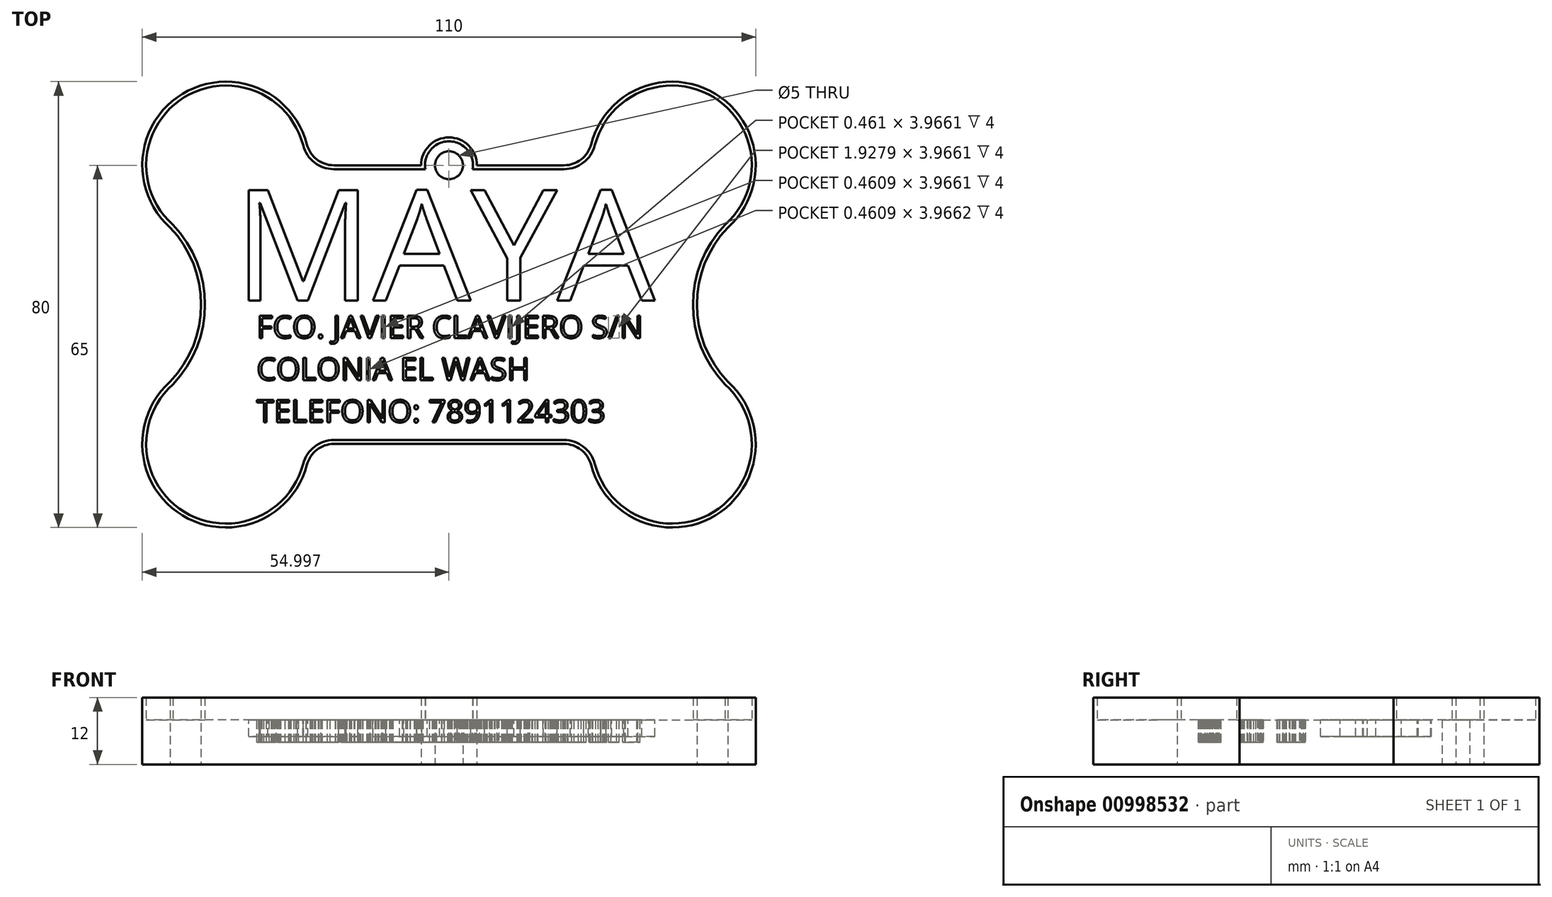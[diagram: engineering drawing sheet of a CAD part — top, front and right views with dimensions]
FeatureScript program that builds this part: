
annotation { "Feature Type Name" : "Feature", "Feature Type Description" : "" }
export const myFeature = defineFeature(function(context is Context, id is Id, definition is map)
    precondition{}
    {
        {
            var Q0;
            Q0=qCreatedBy(makeId("Top.planeOp"),FACE);
            var sketch = newSketch(context, id + "F0", { "sketchPlane" : qUnion([Q0])});
            skLineSegment(sketch, "E0.bottom", {"start": v(-8.45, 26.12) * mm, "end": v(7.19, 26.12) * mm});
            skLineSegment(sketch, "E0.top", {"start": v(-8.45, -23.88) * mm, "end": v(32.82, -23.88) * mm});
            skLineSegment(sketch, "E1", {"start": v(62.19, 16.12) * mm, "end": v(62.19, 14.94) * mm});
            skArc(sketch, "E2", {"start": v(-13.29, 29.87) * mm, "mid": v(-35.61, 38.93) * mm, "end": v(-37.81, 14.94) * mm});
            skArc(sketch, "E3", {"start": v(62.19, 14.94) * mm, "mid": v(59.99, 38.93) * mm, "end": v(37.66, 29.87) * mm});
            skArc(sketch, "E4", {"start": v(-37.81, -12.7) * mm, "mid": v(-35.61, -36.7) * mm, "end": v(-13.29, -27.63) * mm});
            skArc(sketch, "E5", {"start": v(37.66, -27.63) * mm, "mid": v(59.99, -36.7) * mm, "end": v(62.19, -12.7) * mm});
            skArc(sketch, "E6", {"start": v(17.19, 26.12) * mm, "mid": v(12.19, 31.12) * mm, "end": v(7.19, 26.12) * mm});
            skArc(sketch, "E7", {"start": v(-37.81, -12.7) * mm, "mid": v(-32.27, 1.12) * mm, "end": v(-37.81, 14.94) * mm});
            skArc(sketch, "E8", {"start": v(62.19, 14.94) * mm, "mid": v(56.64, 1.12) * mm, "end": v(62.19, -12.7) * mm});
            skCircle(sketch, "E9", {"center": v(12.19, 26.12) * mm, "radius": 2.5 * mm});
            skLineSegment(sketch, "E10.trimOffspring", {"start": v(17.19, 26.12) * mm, "end": v(32.82, 26.12) * mm});
            skPoint(sketch, "E11.visualSharp", {"position": v(-12.81, 26.12) * mm});
            skArc(sketch, "E11.filletArc", {"start": v(-13.29, 29.87) * mm, "mid": v(-11.5, 27.17) * mm, "end": v(-8.45, 26.12) * mm});
            skPoint(sketch, "E12.visualSharp", {"position": v(37.19, 26.12) * mm});
            skArc(sketch, "E12.filletArc", {"start": v(32.82, 26.12) * mm, "mid": v(35.88, 27.17) * mm, "end": v(37.66, 29.87) * mm});
            skPoint(sketch, "E13.visualSharp", {"position": v(-12.81, -23.88) * mm});
            skArc(sketch, "E13.filletArc", {"start": v(-8.45, -23.88) * mm, "mid": v(-11.5, -24.93) * mm, "end": v(-13.29, -27.63) * mm});
            skPoint(sketch, "E14.visualSharp", {"position": v(37.19, -23.88) * mm});
            skArc(sketch, "E14.filletArc", {"start": v(37.66, -27.63) * mm, "mid": v(35.88, -24.93) * mm, "end": v(32.82, -23.88) * mm});
            skSolve(sketch);
        }
        {
            var Q0;
            Q0=makeQuery(id+"F0.imprint","IMPRINT",FACE,{"disambiguationData":[TD([[makeQuery(id+"F0.imprint","IMPRINT",EDGE,{"derivedFrom":sQuery(id+"F0.wireOp",EDGE,"E0.bottom")}),-1.0]])]});
            extrude(context, id + "F1", {"entities" : qUnion([Q0]), "depth" : 8 * mm, "offsetDistance" : 25 * mm, "hasSecondDirectionDraft" : true, "secondDirectionDraftAngle" : 3 * degree});
        }
        {
            var Q0;
            Q0=makeQuery(id+"F1.opExtrude","CAP_FACE",FACE,{"disambiguationData":[OSD([sQuery(id+"F0.wireOp",EDGE,"E0.bottom"),sQuery(id+"F0.wireOp",EDGE,"E0.top"),sQuery(id+"F0.wireOp",EDGE,"E2"),sQuery(id+"F0.wireOp",EDGE,"E3"),sQuery(id+"F0.wireOp",EDGE,"E4"),sQuery(id+"F0.wireOp",EDGE,"E5"),sQuery(id+"F0.wireOp",EDGE,"E6"),sQuery(id+"F0.wireOp",EDGE,"E7"),sQuery(id+"F0.wireOp",EDGE,"E8"),sQuery(id+"F0.wireOp",EDGE,"E9"),sQuery(id+"F0.wireOp",EDGE,"E10.trimOffspring"),sQuery(id+"F0.wireOp",EDGE,"E11.filletArc"),sQuery(id+"F0.wireOp",EDGE,"E12.filletArc"),sQuery(id+"F0.wireOp",EDGE,"E13.filletArc"),sQuery(id+"F0.wireOp",EDGE,"E14.filletArc")])],"isStart":false});
            var sketch = newSketch(context, id + "F2", { "sketchPlane" : qUnion([Q0])});
            skText(sketch, "E15", { "text": "MAYA\n", "fontName": "OpenSans-Regular.ttf"});
            const initialGuessF2  = {"E15": [-0.02645, 0.00187, 1, 0, 0.01994]};
            skSetInitialGuess(sketch, initialGuessF2);
            skSolve(sketch);
        }
        {
            var Q0;
            Q0 = qSketchRegion(id + "F2", true);
            extrude(context, id + "F3", {"entities" : qUnion([Q0]), "operationType" : NewBodyOperationType.REMOVE, "oppositeDirection" : true, "depth" : 3 * mm, "offsetDistance" : 25 * mm});
        }
        {
            var Q0;
            {var subQ0=sQuery(id+"F0.wireOp",EDGE,"E8");var subQ1=sQuery(id+"F0.wireOp",EDGE,"E7");var subQ2=sQuery(id+"F0.wireOp",EDGE,"E6");var subQ3=sQuery(id+"F0.wireOp",EDGE,"E5");var subQ4=sQuery(id+"F0.wireOp",EDGE,"E4");var subQ5=sQuery(id+"F0.wireOp",EDGE,"E9");var subQ6=sQuery(id+"F0.wireOp",EDGE,"E0.bottom");var subQ7=sQuery(id+"F0.wireOp",EDGE,"E3");var subQ8=sQuery(id+"F0.wireOp",EDGE,"E0.top");var subQ9=sQuery(id+"F0.wireOp",EDGE,"E2");var subQ10=sQuery(id+"F0.wireOp",EDGE,"E10.trimOffspring");var subQ11=sQuery(id+"F0.wireOp",EDGE,"E11.filletArc");var subQ12=sQuery(id+"F0.wireOp",EDGE,"E12.filletArc");var subQ13=sQuery(id+"F0.wireOp",EDGE,"E13.filletArc");var subQ14=sQuery(id+"F0.wireOp",EDGE,"E14.filletArc");Q0=makeQuery(id+"F3.boolean.opBoolean","SPLIT",FACE,{"disambiguationData":[TD([makeQuery(id+"F1.opExtrude","SWEPT_FACE",FACE,{"disambiguationData":[OSD([subQ6])]})])],"derivedFrom":makeQuery(id+"F1.opExtrude","CAP_FACE",FACE,{"disambiguationData":[OSD([subQ6,subQ8,subQ9,subQ7,subQ4,subQ3,subQ2,subQ1,subQ0,subQ5,subQ10,subQ11,subQ12,subQ13,subQ14])],"isStart":false})});}
            var sketch = newSketch(context, id + "F4", { "sketchPlane" : qUnion([Q0])});
            skArc(sketch, "E16.0", {"start": v(38.34, -27.45) * mm, "mid": v(59.63, -36.09) * mm, "end": v(61.7, -13.2) * mm});
            skArc(sketch, "E16.1", {"start": v(32.82, -23.18) * mm, "mid": v(36.31, -24.37) * mm, "end": v(38.34, -27.45) * mm});
            skLineSegment(sketch, "E16.2", {"start": v(-8.45, -23.18) * mm, "end": v(32.82, -23.18) * mm});
            skArc(sketch, "E16.3", {"start": v(16.43, 25.42) * mm, "mid": v(12.19, 30.42) * mm, "end": v(7.94, 25.42) * mm});
            skLineSegment(sketch, "E16.4", {"start": v(32.82, 25.42) * mm, "end": v(16.43, 25.42) * mm});
            skArc(sketch, "E16.5", {"start": v(38.34, 29.7) * mm, "mid": v(36.31, 26.61) * mm, "end": v(32.82, 25.42) * mm});
            skArc(sketch, "E16.6", {"start": v(61.7, 15.44) * mm, "mid": v(59.63, 38.33) * mm, "end": v(38.34, 29.7) * mm});
            skLineSegment(sketch, "E16.7", {"start": v(7.94, 25.42) * mm, "end": v(-8.45, 25.42) * mm});
            skArc(sketch, "E16.8", {"start": v(-8.45, 25.42) * mm, "mid": v(-11.94, 26.61) * mm, "end": v(-13.97, 29.7) * mm});
            skArc(sketch, "E16.9", {"start": v(-13.97, 29.7) * mm, "mid": v(-35.26, 38.33) * mm, "end": v(-37.33, 15.44) * mm});
            skArc(sketch, "E16.10", {"start": v(61.7, -13.2) * mm, "mid": v(55.94, 1.12) * mm, "end": v(61.7, 15.44) * mm});
            skArc(sketch, "E16.11", {"start": v(-37.33, 15.44) * mm, "mid": v(-31.57, 1.12) * mm, "end": v(-37.33, -13.2) * mm});
            skArc(sketch, "E16.12", {"start": v(-37.33, -13.2) * mm, "mid": v(-35.26, -36.09) * mm, "end": v(-13.97, -27.45) * mm});
            skArc(sketch, "E16.13", {"start": v(-13.97, -27.45) * mm, "mid": v(-11.94, -24.37) * mm, "end": v(-8.45, -23.18) * mm});
            skSolve(sketch);
        }
        {
            var Q0;
            Q0=makeQuery(id+"F4.imprint","IMPRINT",FACE,{"disambiguationData":[TD([[makeQuery(id+"F4.imprint","IMPRINT",EDGE,{"derivedFrom":sQuery(id+"F4.wireOp",EDGE,"E16.0")}),-1.0]])]});
            extrude(context, id + "F5", {"entities" : qUnion([Q0]), "operationType" : NewBodyOperationType.ADD, "depth" : 4 * mm, "offsetDistance" : 25 * mm});
        }
        {
            var Q0;
            {var subQ0=sQuery(id+"F0.wireOp",EDGE,"E8");var subQ1=sQuery(id+"F0.wireOp",EDGE,"E7");var subQ2=sQuery(id+"F0.wireOp",EDGE,"E6");var subQ3=sQuery(id+"F0.wireOp",EDGE,"E5");var subQ4=sQuery(id+"F0.wireOp",EDGE,"E4");var subQ5=sQuery(id+"F0.wireOp",EDGE,"E9");var subQ6=sQuery(id+"F0.wireOp",EDGE,"E0.bottom");var subQ7=sQuery(id+"F0.wireOp",EDGE,"E3");var subQ8=sQuery(id+"F0.wireOp",EDGE,"E0.top");var subQ9=sQuery(id+"F0.wireOp",EDGE,"E2");var subQ10=sQuery(id+"F0.wireOp",EDGE,"E10.trimOffspring");var subQ11=sQuery(id+"F0.wireOp",EDGE,"E11.filletArc");var subQ12=sQuery(id+"F0.wireOp",EDGE,"E12.filletArc");var subQ13=sQuery(id+"F0.wireOp",EDGE,"E13.filletArc");var subQ14=sQuery(id+"F0.wireOp",EDGE,"E14.filletArc");Q0=makeQuery(id+"F3.boolean.opBoolean","SPLIT",FACE,{"disambiguationData":[TD([makeQuery(id+"F1.opExtrude","SWEPT_FACE",FACE,{"disambiguationData":[OSD([subQ6])]})])],"derivedFrom":makeQuery(id+"F1.opExtrude","CAP_FACE",FACE,{"disambiguationData":[OSD([subQ6,subQ8,subQ9,subQ7,subQ4,subQ3,subQ2,subQ1,subQ0,subQ5,subQ10,subQ11,subQ12,subQ13,subQ14])],"isStart":false})});}
            var sketch = newSketch(context, id + "F6", { "sketchPlane" : qUnion([Q0])});
            skText(sketch, "E17", { "text": "FCO. JAVIER CLAVIJERO S/N\nCOLONIA EL WASH\nTELEFONO: 7891124303", "fontName": "OpenSans-Regular.ttf"});
            const initialGuessF6  = {"E17": [-0.02229, -0.00488, 1, 0, 0.004]};
            skSetInitialGuess(sketch, initialGuessF6);
            skSolve(sketch);
        }
        {
            var Q0;
            Q0 = qSketchRegion(id + "F6", true);
            extrude(context, id + "F7", {"entities" : qUnion([Q0]), "operationType" : NewBodyOperationType.REMOVE, "oppositeDirection" : true, "depth" : 4 * mm, "offsetDistance" : 25 * mm});
        }
        {
            var Q0;
            Q0=qCreatedBy(makeId("Top.planeOp"),FACE);
            var sketch = newSketch(context, id + "F8", { "sketchPlane" : qUnion([Q0])});
            skLineSegment(sketch, "E18.bottom", {"start": v(-69.86, -42.23) * mm, "end": v(-42.76, -42.23) * mm});
            skLineSegment(sketch, "E18.top", {"start": v(-69.86, -50.07) * mm, "end": v(-42.76, -50.07) * mm});
            skLineSegment(sketch, "E18.left", {"start": v(-69.86, -42.23) * mm, "end": v(-69.86, -50.07) * mm});
            skLineSegment(sketch, "E18.right", {"start": v(-42.76, -42.23) * mm, "end": v(-42.76, -50.07) * mm});
            skLineSegment(sketch, "E19.bottom", {"start": v(-24.77, -55.78) * mm, "end": v(44.88, -55.78) * mm});
            skLineSegment(sketch, "E19.top", {"start": v(-24.77, -68.06) * mm, "end": v(44.88, -68.06) * mm});
            skLineSegment(sketch, "E19.left", {"start": v(-24.77, -55.78) * mm, "end": v(-24.77, -68.06) * mm});
            skLineSegment(sketch, "E19.right", {"start": v(44.88, -55.78) * mm, "end": v(44.88, -68.06) * mm});
            skText(sketch, "E20", { "text": "AMOR\n", "fontName": "OpenSans-Regular.ttf"});
            const initialGuessF8  = {"E20": [-0.00423, -0.06573, 1, 0, 0.0055]};
            skSetInitialGuess(sketch, initialGuessF8);
            skSolve(sketch);
        }
        {
            var Q0;
            Q0 = qSketchRegion(id + "F8", true);
            extrude(context, id + "F9", {"entities" : qUnion([Q0]), "operationType" : NewBodyOperationType.REMOVE, "depth" : 5 * mm, "offsetDistance" : 25 * mm});
        }
    });
